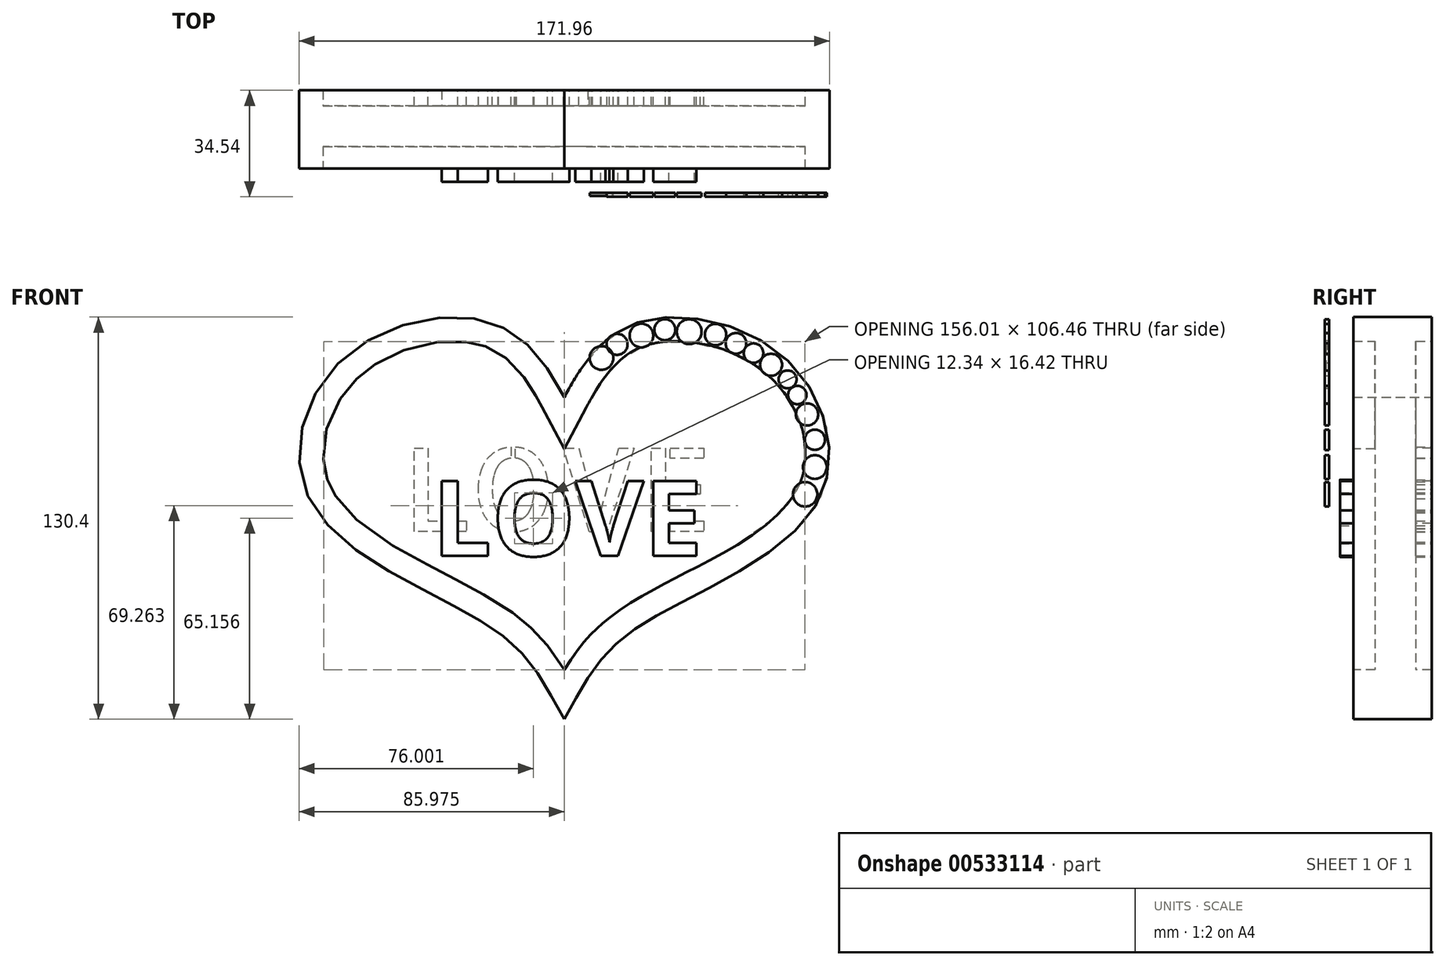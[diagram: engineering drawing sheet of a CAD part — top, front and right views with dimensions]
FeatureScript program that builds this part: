
annotation { "Feature Type Name" : "Feature", "Feature Type Description" : "" }
export const myFeature = defineFeature(function(context is Context, id is Id, definition is map)
    precondition{}
    {
        {
            var Q0;
            Q0=qCreatedBy(makeId("Front.planeOp"),FACE);
            var sketch = newSketch(context, id + "F0", { "sketchPlane" : qUnion([Q0])});
            skFitSpline(sketch, "E0", {"points": [v(0, 26.98) * mm, v(25.34, 51.6) * mm, v(72.14, 39.09) * mm, v(83.43, -4.48) * mm, v(41.88, -37.56) * mm, v(14.45, -55.3) * mm, v(0, -77.5) * mm], "startDerivative": vector(121.69, 230.66) * mm, "endDerivative": vector(-99.84, -179.7) * mm});
            skFitSpline(sketch, "E1.MirrorCS", {"points": [v(0, 26.98) * mm, v(-25.34, 51.6) * mm, v(-72.14, 39.09) * mm, v(-83.43, -4.48) * mm, v(-41.88, -37.56) * mm, v(-14.45, -55.3) * mm, v(0, -77.5) * mm], "startDerivative": vector(-121.69, 230.66) * mm, "endDerivative": vector(99.84, -179.7) * mm});
            skSolve(sketch);
        }
        {
            var Q0;
            Q0=makeQuery(id+"F0.imprint","IMPRINT",FACE,{"disambiguationData":[TD([[makeQuery(id+"F0.imprint","IMPRINT",EDGE,{"derivedFrom":sQuery(id+"F0.wireOp",EDGE,"E0")}),-1.0]])]});
            extrude(context, id + "F1", {"entities" : qUnion([Q0]), "depth" : 25.4 * mm, "offsetDistance" : 25.4 * mm});
        }
        {
            var Q0;
            Q0=makeQuery(id+"F1.opExtrude","CAP_FACE",FACE,{"disambiguationData":[OSD([sQuery(id+"F0.wireOp",EDGE,"E0"),sQuery(id+"F0.wireOp",EDGE,"E1.MirrorCS")])],"isStart":false});
            var sketch = newSketch(context, id + "F2", { "sketchPlane" : qUnion([Q0])});
            skFitSpline(sketch, "E2.0", {"points": [v(0, 10.1) * mm, v(0.67, 11.38) * mm, v(1.68, 13.28) * mm, v(3.02, 15.82) * mm, v(4.02, 17.73) * mm, v(4.86, 19.32) * mm, v(5.53, 20.59) * mm, v(6.03, 21.54) * mm, v(6.45, 22.33) * mm, v(6.74, 22.89) * mm, v(6.89, 23.17) * mm, v(6.97, 23.33) * mm, v(7.05, 23.47) * mm, v(7.15, 23.66) * mm, v(7.3, 23.96) * mm, v(7.5, 24.33) * mm, v(7.74, 24.77) * mm, v(8.06, 25.35) * mm, v(8.46, 26.06) * mm, v(9.1, 27.18) * mm, v(9.9, 28.53) * mm, v(10.86, 30.09) * mm, v(12.16, 32.05) * mm, v(13.81, 34.32) * mm, v(15.84, 36.72) * mm, v(17.92, 38.78) * mm, v(20.07, 40.53) * mm, v(22.33, 41.97) * mm, v(24.34, 42.95) * mm, v(26.07, 43.6) * mm, v(27.43, 44.01) * mm, v(28.88, 44.36) * mm, v(30.95, 44.74) * mm, v(33.74, 45.03) * mm, v(37.35, 45.06) * mm, v(41.13, 44.76) * mm, v(46.31, 43.91) * mm, v(51.54, 42.4) * mm, v(56.53, 40.27) * mm, v(60.09, 38.37) * mm, v(62.85, 36.55) * mm, v(64.9, 34.97) * mm, v(66.36, 33.72) * mm, v(67.73, 32.41) * mm, v(69.47, 30.57) * mm, v(71.46, 28.09) * mm, v(73.51, 24.9) * mm, v(75.79, 20.42) * mm, v(77.31, 15.74) * mm, v(78.04, 11.09) * mm, v(78.17, 7.67) * mm, v(77.95, 4.93) * mm, v(77.56, 2.83) * mm, v(77.18, 1.3) * mm, v(76.78, 0.06) * mm, v(76.4, -0.9) * mm, v(76, -1.85) * mm, v(75.41, -3.02) * mm, v(74.32, -4.9) * mm, v(72.65, -7.24) * mm, v(69.35, -10.95) * mm, v(64.16, -15.46) * mm, v(56.72, -20.5) * mm, v(50, -24.38) * mm, v(44.58, -27.29) * mm, v(40.55, -29.38) * mm, v(36.64, -31.4) * mm, v(32.9, -33.36) * mm, v(29.3, -35.27) * mm, v(24.72, -37.82) * mm, v(20.41, -40.43) * mm, v(16.37, -43.24) * mm, v(13.95, -45.1) * mm, v(12.1, -46.68) * mm, v(10.73, -47.9) * mm, v(9.42, -49.18) * mm, v(7.71, -50.95) * mm, v(5.74, -53.24) * mm, v(3.58, -56.07) * mm, v(1.6, -58.97) * mm, v(-0.86, -62.87) * mm, v(-3.67, -67.8) * mm, v(-5.8, -71.73) * mm, v(-6.88, -73.67) * mm]});
            skFitSpline(sketch, "E2.1", {"points": [v(0, 10.1) * mm, v(-0.67, 11.38) * mm, v(-1.68, 13.28) * mm, v(-3.02, 15.82) * mm, v(-4.02, 17.73) * mm, v(-4.86, 19.32) * mm, v(-5.53, 20.59) * mm, v(-6.03, 21.54) * mm, v(-6.45, 22.33) * mm, v(-6.74, 22.89) * mm, v(-6.89, 23.17) * mm, v(-6.97, 23.33) * mm, v(-7.05, 23.47) * mm, v(-7.15, 23.66) * mm, v(-7.3, 23.96) * mm, v(-7.5, 24.33) * mm, v(-7.74, 24.77) * mm, v(-8.06, 25.35) * mm, v(-8.46, 26.06) * mm, v(-9.1, 27.18) * mm, v(-9.9, 28.53) * mm, v(-10.86, 30.09) * mm, v(-12.16, 32.05) * mm, v(-13.81, 34.32) * mm, v(-15.84, 36.72) * mm, v(-17.92, 38.78) * mm, v(-20.07, 40.53) * mm, v(-22.33, 41.97) * mm, v(-24.34, 42.95) * mm, v(-26.07, 43.6) * mm, v(-27.43, 44.01) * mm, v(-28.88, 44.36) * mm, v(-30.95, 44.74) * mm, v(-33.74, 45.03) * mm, v(-37.35, 45.06) * mm, v(-41.13, 44.76) * mm, v(-46.31, 43.91) * mm, v(-51.54, 42.4) * mm, v(-56.53, 40.27) * mm, v(-60.09, 38.37) * mm, v(-62.85, 36.55) * mm, v(-64.9, 34.97) * mm, v(-66.36, 33.72) * mm, v(-67.73, 32.41) * mm, v(-69.47, 30.57) * mm, v(-71.46, 28.09) * mm, v(-73.51, 24.9) * mm, v(-75.79, 20.42) * mm, v(-77.31, 15.74) * mm, v(-78.04, 11.09) * mm, v(-78.17, 7.67) * mm, v(-77.95, 4.93) * mm, v(-77.56, 2.83) * mm, v(-77.18, 1.3) * mm, v(-76.78, 0.06) * mm, v(-76.4, -0.9) * mm, v(-76, -1.85) * mm, v(-75.41, -3.02) * mm, v(-74.32, -4.9) * mm, v(-72.65, -7.24) * mm, v(-69.35, -10.95) * mm, v(-64.16, -15.46) * mm, v(-56.72, -20.5) * mm, v(-50, -24.38) * mm, v(-44.58, -27.29) * mm, v(-40.55, -29.38) * mm, v(-36.64, -31.4) * mm, v(-32.9, -33.36) * mm, v(-29.3, -35.27) * mm, v(-24.72, -37.82) * mm, v(-20.41, -40.43) * mm, v(-16.37, -43.24) * mm, v(-13.95, -45.1) * mm, v(-12.1, -46.68) * mm, v(-10.73, -47.9) * mm, v(-9.42, -49.18) * mm, v(-7.71, -50.95) * mm, v(-5.74, -53.24) * mm, v(-3.58, -56.07) * mm, v(-1.6, -58.97) * mm, v(0.86, -62.87) * mm, v(3.67, -67.8) * mm, v(5.8, -71.73) * mm, v(6.88, -73.67) * mm]});
            skLineSegment(sketch, "E3", {"start": v(7.17, 23.67) * mm, "end": v(0, 17.62) * mm});
            skLineSegment(sketch, "E4", {"start": v(0, 17.62) * mm, "end": v(-7.19, 23.72) * mm});
            skSolve(sketch);
        }
        {
            var Q0;
            {var subQ0=sQuery(id+"F2.wireOp",EDGE,"E2.1");var subQ1=sQuery(id+"F2.wireOp",EDGE,"E2.0");var subQ2=makeQuery(id+"F2.imprint","INTERSECT",VERTEX,{"derivedFrom":[subQ1,subQ0]});Q0=makeQuery(id+"F2.imprint","IMPRINT",FACE,{"disambiguationData":[TD([[makeQuery(id+"F2.imprint","IMPRINT",EDGE,{"disambiguationData":[TD([[subQ2,1.0]])],"derivedFrom":subQ1}),-1.0]])]});}
            extrude(context, id + "F3", {"entities" : qUnion([Q0]), "operationType" : NewBodyOperationType.REMOVE, "oppositeDirection" : true, "depth" : 25.4 * mm, "offsetDistance" : 25.4 * mm});
        }
        {
            var Q0;
            Q0=qCreatedBy(makeId("Front.planeOp"),FACE);
            var sketch = newSketch(context, id + "F4", { "sketchPlane" : qUnion([Q0])});
            skText(sketch, "E5", { "text": "LOVE \n\n", "fontName": "AllertaStencil-Regular.ttf"});
            const initialGuessF4  = {"E5": [-0.05207, -0.01661, 1, 0, 0.02704]};
            skSetInitialGuess(sketch, initialGuessF4);
            skSolve(sketch);
        }
        {
            var Q0;
            Q0 = qSketchRegion(id + "F4", true);
            extrude(context, id + "F5", {"entities" : qUnion([Q0]), "operationType" : NewBodyOperationType.ADD, "depth" : 25.4 * mm, "offsetDistance" : 25.4 * mm});
        }
        {
            var Q0;
            Q0=qCreatedBy(makeId("Front.planeOp"),FACE);
            var sketch = newSketch(context, id + "F6", { "sketchPlane" : qUnion([Q0])});
            skText(sketch, "E6", { "text": "LOVE", "fontName": "OpenSans-Bold.ttf"});
            const initialGuessF6  = {"E6": [-0.0428, -0.02454, 1, 0, 0.02454]};
            skSetInitialGuess(sketch, initialGuessF6);
            skSolve(sketch);
        }
        {
            var Q0;
            Q0 = qSketchRegion(id + "F6", true);
            extrude(context, id + "F7", {"entities" : qUnion([Q0]), "depth" : 29.72 * mm, "offsetDistance" : 25.4 * mm});
        }
        {
            var Q0;
            {var subQ0=sQuery(id+"F2.wireOp",EDGE,"E2.1");var subQ1=sQuery(id+"F2.wireOp",EDGE,"E2.0");var subQ2=makeQuery(id+"F2.imprint","INTERSECT",VERTEX,{"derivedFrom":[subQ1,subQ0]});Q0=makeQuery(id+"F2.imprint","IMPRINT",FACE,{"disambiguationData":[TD([[makeQuery(id+"F2.imprint","IMPRINT",EDGE,{"disambiguationData":[TD([[subQ2,1.0]])],"derivedFrom":subQ1}),-1.0]])]});}
            extrude(context, id + "F8", {"entities" : qUnion([Q0]), "operationType" : NewBodyOperationType.ADD, "oppositeDirection" : true, "depth" : 20.32 * mm, "offsetDistance" : 25.4 * mm});
        }
        {
            var Q0;
            {var subQ0=sQuery(id+"F2.wireOp",EDGE,"E2.1");var subQ1=sQuery(id+"F2.wireOp",EDGE,"E2.0");var subQ2=makeQuery(id+"F2.imprint","INTERSECT",VERTEX,{"derivedFrom":[subQ1,subQ0]});Q0=makeQuery(id+"F2.imprint","IMPRINT",FACE,{"disambiguationData":[TD([[makeQuery(id+"F2.imprint","IMPRINT",EDGE,{"disambiguationData":[TD([[subQ2,1.0]])],"derivedFrom":subQ1}),-1.0]])]});}
            extrude(context, id + "F9", {"entities" : qUnion([Q0]), "operationType" : NewBodyOperationType.REMOVE, "oppositeDirection" : true, "depth" : 7.11 * mm, "offsetDistance" : 25.4 * mm});
        }
        {
            var Q0;
            Q0=makeQuery(id+"F9.boolean.opBoolean","SPLIT",BODY,{"disambiguationData":[OD(3.0)],"derivedFrom":makeQuery(id+"F1.opExtrude","SWEPT_BODY",BODY,{"disambiguationData":[OSD([sQuery(id+"F0.wireOp",EDGE,"E0"),sQuery(id+"F0.wireOp",EDGE,"E1.MirrorCS")])]})});
            var Q1;
            Q1=makeQuery(id+"F9.boolean.opBoolean","SPLIT",BODY,{"disambiguationData":[OD(2.0)],"derivedFrom":makeQuery(id+"F1.opExtrude","SWEPT_BODY",BODY,{"disambiguationData":[OSD([sQuery(id+"F0.wireOp",EDGE,"E0"),sQuery(id+"F0.wireOp",EDGE,"E1.MirrorCS")])]})});
            var Q2;
            Q2=makeQuery(id+"F9.boolean.opBoolean","SPLIT",BODY,{"disambiguationData":[OD(1.0)],"derivedFrom":makeQuery(id+"F1.opExtrude","SWEPT_BODY",BODY,{"disambiguationData":[OSD([sQuery(id+"F0.wireOp",EDGE,"E0"),sQuery(id+"F0.wireOp",EDGE,"E1.MirrorCS")])]})});
            var Q3;
            Q3=makeQuery(id+"F9.boolean.opBoolean","SPLIT",BODY,{"disambiguationData":[OD(4.0)],"derivedFrom":makeQuery(id+"F1.opExtrude","SWEPT_BODY",BODY,{"disambiguationData":[OSD([sQuery(id+"F0.wireOp",EDGE,"E0"),sQuery(id+"F0.wireOp",EDGE,"E1.MirrorCS")])]})});
            transform(context, id + "F10", {"entities" : qUnion([Q0, Q1, Q2, Q3]), "transformType" : TransformType.TRANSLATION_3D, "dx" : 0 * mm, "dy" : 7.87 * mm, "dz" : 0 * mm, "makeCopy" : false});
        }
        {
            var Q0;
            Q0=makeQuery(id+"F2.imprint","IMPRINT",FACE,{"disambiguationData":[TD([[makeQuery(id+"F2.imprint","IMPRINT",EDGE,{"derivedFrom":makeQuery(id+"F1.opExtrude","CAP_EDGE",EDGE,{"disambiguationData":[OSD([sQuery(id+"F0.wireOp",EDGE,"E0")])],"isStart":false})}),-1.0]])]});
            var sketch = newSketch(context, id + "F11", { "sketchPlane" : qUnion([Q0])});
            skCircle(sketch, "E7", {"center": v(25.01, 46.92) * mm, "radius": 3.84 * mm});
            skCircle(sketch, "E8", {"center": v(32.59, 48.81) * mm, "radius": 3.42 * mm});
            skCircle(sketch, "E9", {"center": v(40.48, 48.18) * mm, "radius": 4.02 * mm});
            skCircle(sketch, "E10", {"center": v(49.01, 47.23) * mm, "radius": 3.47 * mm});
            skCircle(sketch, "E11", {"center": v(55.64, 44.39) * mm, "radius": 3.36 * mm});
            skCircle(sketch, "E12", {"center": v(61.33, 41.23) * mm, "radius": 3.16 * mm});
            skCircle(sketch, "E13", {"center": v(67.01, 37.44) * mm, "radius": 3.57 * mm});
            skCircle(sketch, "E14", {"center": v(72.38, 32.7) * mm, "radius": 2.91 * mm});
            skCircle(sketch, "E15", {"center": v(75.54, 27.65) * mm, "radius": 2.98 * mm});
            skCircle(sketch, "E16", {"center": v(78.7, 21.34) * mm, "radius": 3.6 * mm});
            skCircle(sketch, "E17", {"center": v(81.22, 13.13) * mm, "radius": 3.3 * mm});
            skCircle(sketch, "E18", {"center": v(17.12, 44.07) * mm, "radius": 3.4 * mm});
            skCircle(sketch, "E19", {"center": v(12.06, 39.65) * mm, "radius": 3.84 * mm});
            skCircle(sketch, "E20", {"center": v(81.22, 4.28) * mm, "radius": 3.84 * mm});
            skCircle(sketch, "E21", {"center": v(78.06, -4.56) * mm, "radius": 3.96 * mm});
            skSolve(sketch);
        }
        {
            var Q0;
            {var subQ0=sQuery(id+"F11.wireOp",EDGE,"E19");var subQ1=sQuery(id+"F11.wireOp",EDGE,"E18");var subQ2=makeQuery(id+"F11.imprint","INTERSECT",VERTEX,{"disambiguationData":[OD(0.0)],"derivedFrom":[subQ1,subQ0]});Q0=makeQuery(id+"F11.imprint","IMPRINT",FACE,{"disambiguationData":[TD([[makeQuery(id+"F11.imprint","IMPRINT",EDGE,{"disambiguationData":[TD([[subQ2,-1.0]])],"derivedFrom":subQ1}),-1.0]])]});}
            extrude(context, id + "F12", {"entities" : qUnion([Q0]), "operationType" : NewBodyOperationType.ADD, "depth" : 1.02 * mm, "offsetDistance" : 25.4 * mm});
        }
        {
            var Q0;
            {var subQ0=sQuery(id+"F11.wireOp",EDGE,"E19");var subQ1=sQuery(id+"F11.wireOp",EDGE,"E18");var subQ2=makeQuery(id+"F11.imprint","INTERSECT",VERTEX,{"disambiguationData":[OD(0.0)],"derivedFrom":[subQ1,subQ0]});Q0=makeQuery(id+"F11.imprint","IMPRINT",FACE,{"disambiguationData":[TD([[makeQuery(id+"F11.imprint","IMPRINT",EDGE,{"disambiguationData":[TD([[subQ2,1.0]])],"derivedFrom":subQ1}),1.0]])]});}
            extrude(context, id + "F13", {"entities" : qUnion([Q0]), "operationType" : NewBodyOperationType.ADD, "depth" : 0.76 * mm, "offsetDistance" : 25.4 * mm});
        }
        {
            var Q0;
            {var subQ0=sQuery(id+"F11.wireOp",EDGE,"E7");var subQ1=sQuery(id+"F2.wireOp",EDGE,"E2.0");var subQ2=makeQuery(id+"F2.imprint","IMPRINT",EDGE,{"disambiguationData":[TD([[makeQuery(id+"F2.imprint","INTERSECT",VERTEX,{"derivedFrom":[subQ1,sQuery(id+"F2.wireOp",EDGE,"E2.1")]}),1.0]])],"derivedFrom":subQ1});var subQ3=makeQuery(id+"F11.imprint","INTERSECT",VERTEX,{"disambiguationData":[OD(0.0)],"derivedFrom":[subQ2,subQ0]});Q0=makeQuery(id+"F11.imprint","IMPRINT",FACE,{"disambiguationData":[TD([[makeQuery(id+"F11.imprint","IMPRINT",EDGE,{"disambiguationData":[TD([[subQ3,1.0]])],"derivedFrom":subQ0}),1.0]])]});}
            extrude(context, id + "F14", {"entities" : qUnion([Q0]), "operationType" : NewBodyOperationType.ADD, "depth" : 1.27 * mm, "offsetDistance" : 25.4 * mm});
        }
        {
            var Q0;
            {var subQ0=sQuery(id+"F11.wireOp",EDGE,"E9");var subQ1=sQuery(id+"F2.wireOp",EDGE,"E2.0");var subQ2=makeQuery(id+"F2.imprint","IMPRINT",EDGE,{"disambiguationData":[TD([[makeQuery(id+"F2.imprint","INTERSECT",VERTEX,{"derivedFrom":[subQ1,sQuery(id+"F2.wireOp",EDGE,"E2.1")]}),1.0]])],"derivedFrom":subQ1});var subQ3=makeQuery(id+"F11.imprint","INTERSECT",VERTEX,{"disambiguationData":[OD(0.0)],"derivedFrom":[subQ2,subQ0]});Q0=makeQuery(id+"F11.imprint","IMPRINT",FACE,{"disambiguationData":[TD([[makeQuery(id+"F11.imprint","IMPRINT",EDGE,{"disambiguationData":[TD([[subQ3,-1.0]])],"derivedFrom":subQ0}),1.0]])]});}
            extrude(context, id + "F15", {"entities" : qUnion([Q0]), "operationType" : NewBodyOperationType.ADD, "depth" : 1.27 * mm, "offsetDistance" : 25.4 * mm});
        }
        {
            var Q0;
            {var subQ0=sQuery(id+"F11.wireOp",EDGE,"E21");var subQ1=sQuery(id+"F2.wireOp",EDGE,"E2.0");var subQ2=makeQuery(id+"F2.imprint","IMPRINT",EDGE,{"disambiguationData":[TD([[makeQuery(id+"F2.imprint","INTERSECT",VERTEX,{"derivedFrom":[subQ1,sQuery(id+"F2.wireOp",EDGE,"E2.1")]}),1.0]])],"derivedFrom":subQ1});var subQ3=makeQuery(id+"F11.imprint","INTERSECT",VERTEX,{"disambiguationData":[OD(0.0)],"derivedFrom":[subQ2,subQ0]});Q0=makeQuery(id+"F11.imprint","IMPRINT",FACE,{"disambiguationData":[TD([[makeQuery(id+"F11.imprint","IMPRINT",EDGE,{"disambiguationData":[TD([[subQ3,-1.0]])],"derivedFrom":subQ0}),1.0]])]});}
            extrude(context, id + "F16", {"entities" : qUnion([Q0]), "operationType" : NewBodyOperationType.ADD, "depth" : 1.27 * mm, "offsetDistance" : 25.4 * mm});
        }
        {
            var Q0;
            {var subQ0=sQuery(id+"F11.wireOp",EDGE,"E20");var subQ1=sQuery(id+"F2.wireOp",EDGE,"E2.0");var subQ2=makeQuery(id+"F2.imprint","IMPRINT",EDGE,{"disambiguationData":[TD([[makeQuery(id+"F2.imprint","INTERSECT",VERTEX,{"derivedFrom":[subQ1,sQuery(id+"F2.wireOp",EDGE,"E2.1")]}),1.0]])],"derivedFrom":subQ1});var subQ3=makeQuery(id+"F11.imprint","INTERSECT",VERTEX,{"disambiguationData":[OD(0.0)],"derivedFrom":[subQ2,subQ0]});Q0=makeQuery(id+"F11.imprint","IMPRINT",FACE,{"disambiguationData":[TD([[makeQuery(id+"F11.imprint","IMPRINT",EDGE,{"disambiguationData":[TD([[subQ3,-1.0]])],"derivedFrom":subQ0}),1.0]])]});}
            extrude(context, id + "F17", {"entities" : qUnion([Q0]), "operationType" : NewBodyOperationType.ADD, "depth" : 1.27 * mm, "offsetDistance" : 25.4 * mm});
        }
        {
            var Q0;
            Q0=makeQuery(id+"F11.imprint","IMPRINT",FACE,{"disambiguationData":[TD([[makeQuery(id+"F11.imprint","IMPRINT",EDGE,{"derivedFrom":sQuery(id+"F11.wireOp",EDGE,"E17")}),1.0]])]});
            extrude(context, id + "F18", {"entities" : qUnion([Q0]), "operationType" : NewBodyOperationType.ADD, "depth" : 1.27 * mm, "offsetDistance" : 25.4 * mm});
        }
        {
            var Q0;
            {var subQ0=sQuery(id+"F11.wireOp",EDGE,"E16");var subQ1=sQuery(id+"F2.wireOp",EDGE,"E2.0");var subQ2=makeQuery(id+"F2.imprint","IMPRINT",EDGE,{"disambiguationData":[TD([[makeQuery(id+"F2.imprint","INTERSECT",VERTEX,{"derivedFrom":[subQ1,sQuery(id+"F2.wireOp",EDGE,"E2.1")]}),1.0]])],"derivedFrom":subQ1});var subQ3=makeQuery(id+"F11.imprint","INTERSECT",VERTEX,{"disambiguationData":[OD(0.0)],"derivedFrom":[subQ2,subQ0]});Q0=makeQuery(id+"F11.imprint","IMPRINT",FACE,{"disambiguationData":[TD([[makeQuery(id+"F11.imprint","IMPRINT",EDGE,{"disambiguationData":[TD([[subQ3,1.0]])],"derivedFrom":subQ0}),1.0]])]});}
            extrude(context, id + "F19", {"entities" : qUnion([Q0]), "operationType" : NewBodyOperationType.ADD, "depth" : 1.27 * mm, "offsetDistance" : 25.4 * mm});
        }
        {
            var Q0;
            Q0=makeQuery(id+"F11.imprint","IMPRINT",FACE,{"disambiguationData":[TD([[makeQuery(id+"F11.imprint","IMPRINT",EDGE,{"derivedFrom":sQuery(id+"F11.wireOp",EDGE,"E15")}),1.0]])]});
            extrude(context, id + "F20", {"entities" : qUnion([Q0]), "operationType" : NewBodyOperationType.ADD, "depth" : 1.27 * mm, "offsetDistance" : 25.4 * mm});
        }
        {
            var Q0;
            Q0=makeQuery(id+"F11.imprint","IMPRINT",FACE,{"disambiguationData":[TD([[makeQuery(id+"F11.imprint","IMPRINT",EDGE,{"derivedFrom":sQuery(id+"F11.wireOp",EDGE,"E14")}),1.0]])]});
            extrude(context, id + "F21", {"entities" : qUnion([Q0]), "operationType" : NewBodyOperationType.ADD, "depth" : 1.27 * mm, "offsetDistance" : 25.4 * mm});
        }
        {
            var Q0;
            {var subQ0=sQuery(id+"F11.wireOp",EDGE,"E13");var subQ1=sQuery(id+"F2.wireOp",EDGE,"E2.0");var subQ2=makeQuery(id+"F2.imprint","IMPRINT",EDGE,{"disambiguationData":[TD([[makeQuery(id+"F2.imprint","INTERSECT",VERTEX,{"derivedFrom":[subQ1,sQuery(id+"F2.wireOp",EDGE,"E2.1")]}),1.0]])],"derivedFrom":subQ1});var subQ3=makeQuery(id+"F11.imprint","INTERSECT",VERTEX,{"disambiguationData":[OD(0.0)],"derivedFrom":[subQ2,subQ0]});Q0=makeQuery(id+"F11.imprint","IMPRINT",FACE,{"disambiguationData":[TD([[makeQuery(id+"F11.imprint","IMPRINT",EDGE,{"disambiguationData":[TD([[subQ3,1.0]])],"derivedFrom":subQ0}),1.0]])]});}
            extrude(context, id + "F22", {"entities" : qUnion([Q0]), "operationType" : NewBodyOperationType.ADD, "depth" : 1.27 * mm, "offsetDistance" : 25.4 * mm});
        }
        {
            var Q0;
            {var subQ0=sQuery(id+"F11.wireOp",EDGE,"E12");var subQ1=sQuery(id+"F11.wireOp",EDGE,"E11");var subQ2=makeQuery(id+"F11.imprint","INTERSECT",VERTEX,{"disambiguationData":[OD(0.0)],"derivedFrom":[subQ1,subQ0]});Q0=makeQuery(id+"F11.imprint","IMPRINT",FACE,{"disambiguationData":[TD([[makeQuery(id+"F11.imprint","IMPRINT",EDGE,{"disambiguationData":[TD([[subQ2,-1.0]])],"derivedFrom":subQ1}),-1.0]])]});}
            extrude(context, id + "F23", {"entities" : qUnion([Q0]), "operationType" : NewBodyOperationType.ADD, "depth" : 1.27 * mm, "offsetDistance" : 25.4 * mm});
        }
        {
            var Q0;
            {var subQ0=sQuery(id+"F11.wireOp",EDGE,"E12");var subQ1=sQuery(id+"F11.wireOp",EDGE,"E11");var subQ2=makeQuery(id+"F11.imprint","INTERSECT",VERTEX,{"disambiguationData":[OD(0.0)],"derivedFrom":[subQ1,subQ0]});Q0=makeQuery(id+"F11.imprint","IMPRINT",FACE,{"disambiguationData":[TD([[makeQuery(id+"F11.imprint","IMPRINT",EDGE,{"disambiguationData":[TD([[subQ2,1.0]])],"derivedFrom":subQ1}),1.0]])]});}
            extrude(context, id + "F24", {"entities" : qUnion([Q0]), "operationType" : NewBodyOperationType.ADD, "depth" : 1.27 * mm, "offsetDistance" : 25.4 * mm});
        }
        {
            var Q0;
            Q0=makeQuery(id+"F11.imprint","IMPRINT",FACE,{"disambiguationData":[TD([[makeQuery(id+"F11.imprint","IMPRINT",EDGE,{"derivedFrom":sQuery(id+"F11.wireOp",EDGE,"E10")}),1.0]])]});
            extrude(context, id + "F25", {"entities" : qUnion([Q0]), "operationType" : NewBodyOperationType.ADD, "depth" : 1.27 * mm, "offsetDistance" : 25.4 * mm});
        }
        {
            var Q0;
            {var subQ0=sQuery(id+"F11.wireOp",EDGE,"E19");var subQ1=sQuery(id+"F11.wireOp",EDGE,"E18");var subQ2=makeQuery(id+"F11.imprint","INTERSECT",VERTEX,{"disambiguationData":[OD(0.0)],"derivedFrom":[subQ1,subQ0]});Q0=makeQuery(id+"F11.imprint","IMPRINT",FACE,{"disambiguationData":[TD([[makeQuery(id+"F11.imprint","IMPRINT",EDGE,{"disambiguationData":[TD([[subQ2,1.0]])],"derivedFrom":subQ1}),1.0]])]});}
            extrude(context, id + "F26", {"entities" : qUnion([Q0]), "operationType" : NewBodyOperationType.ADD, "depth" : 1.27 * mm, "offsetDistance" : 25.4 * mm});
        }
        {
            var Q0;
            {var subQ0=sQuery(id+"F11.wireOp",EDGE,"E19");var subQ1=sQuery(id+"F11.wireOp",EDGE,"E18");var subQ2=makeQuery(id+"F11.imprint","INTERSECT",VERTEX,{"disambiguationData":[OD(0.0)],"derivedFrom":[subQ1,subQ0]});Q0=makeQuery(id+"F11.imprint","IMPRINT",FACE,{"disambiguationData":[TD([[makeQuery(id+"F11.imprint","IMPRINT",EDGE,{"disambiguationData":[TD([[subQ2,1.0]])],"derivedFrom":subQ1}),1.0]])]});}
            extrude(context, id + "F27", {"entities" : qUnion([Q0]), "operationType" : NewBodyOperationType.ADD, "depth" : 1.27 * mm, "offsetDistance" : 25.4 * mm});
        }
        {
            var Q0;
            {var subQ0=sQuery(id+"F11.wireOp",EDGE,"E19");var subQ1=sQuery(id+"F11.wireOp",EDGE,"E18");var subQ2=makeQuery(id+"F11.imprint","INTERSECT",VERTEX,{"disambiguationData":[OD(0.0)],"derivedFrom":[subQ1,subQ0]});Q0=makeQuery(id+"F11.imprint","IMPRINT",FACE,{"disambiguationData":[TD([[makeQuery(id+"F11.imprint","IMPRINT",EDGE,{"disambiguationData":[TD([[subQ2,1.0]])],"derivedFrom":subQ1}),1.0]])]});}
            extrude(context, id + "F28", {"entities" : qUnion([Q0]), "operationType" : NewBodyOperationType.ADD, "depth" : 1.27 * mm, "offsetDistance" : 25.4 * mm});
        }
        {
            var Q0;
            {var subQ0=sQuery(id+"F11.wireOp",EDGE,"E19");var subQ1=sQuery(id+"F11.wireOp",EDGE,"E18");var subQ2=makeQuery(id+"F11.imprint","INTERSECT",VERTEX,{"disambiguationData":[OD(0.0)],"derivedFrom":[subQ1,subQ0]});Q0=makeQuery(id+"F11.imprint","IMPRINT",FACE,{"disambiguationData":[TD([[makeQuery(id+"F11.imprint","IMPRINT",EDGE,{"disambiguationData":[TD([[subQ2,1.0]])],"derivedFrom":subQ1}),1.0]])]});}
            extrude(context, id + "F29", {"entities" : qUnion([Q0]), "operationType" : NewBodyOperationType.ADD, "depth" : 0.91 * mm, "offsetDistance" : 25.4 * mm});
        }
        {
            var Q0;
            Q0=makeQuery(id+"F11.imprint","IMPRINT",FACE,{"disambiguationData":[TD([[makeQuery(id+"F11.imprint","IMPRINT",EDGE,{"derivedFrom":sQuery(id+"F11.wireOp",EDGE,"E8")}),1.0]])]});
            extrude(context, id + "F30", {"entities" : qUnion([Q0]), "operationType" : NewBodyOperationType.ADD, "depth" : 1.27 * mm, "offsetDistance" : 25.4 * mm});
        }
        {
            var Q0;
            {var subQ0=sQuery(id+"F11.wireOp",EDGE,"E12");var subQ1=sQuery(id+"F11.wireOp",EDGE,"E11");var subQ2=makeQuery(id+"F11.imprint","INTERSECT",VERTEX,{"disambiguationData":[OD(0.0)],"derivedFrom":[subQ1,subQ0]});Q0=makeQuery(id+"F11.imprint","IMPRINT",FACE,{"disambiguationData":[TD([[makeQuery(id+"F11.imprint","IMPRINT",EDGE,{"disambiguationData":[TD([[subQ2,1.0]])],"derivedFrom":subQ1}),1.0]])]});}
            extrude(context, id + "F31", {"entities" : qUnion([Q0]), "operationType" : NewBodyOperationType.ADD, "depth" : 1.27 * mm, "offsetDistance" : 25.4 * mm});
        }
        {
            var Q0;
            {var subQ0=sQuery(id+"F11.wireOp",EDGE,"E12");var subQ1=sQuery(id+"F11.wireOp",EDGE,"E11");var subQ2=makeQuery(id+"F11.imprint","INTERSECT",VERTEX,{"disambiguationData":[OD(0.0)],"derivedFrom":[subQ1,subQ0]});Q0=makeQuery(id+"F11.imprint","IMPRINT",FACE,{"disambiguationData":[TD([[makeQuery(id+"F11.imprint","IMPRINT",EDGE,{"disambiguationData":[TD([[subQ2,1.0]])],"derivedFrom":subQ1}),1.0]])]});}
            extrude(context, id + "F32", {"entities" : qUnion([Q0]), "operationType" : NewBodyOperationType.ADD, "depth" : 1.27 * mm, "offsetDistance" : 25.4 * mm});
        }
    });
